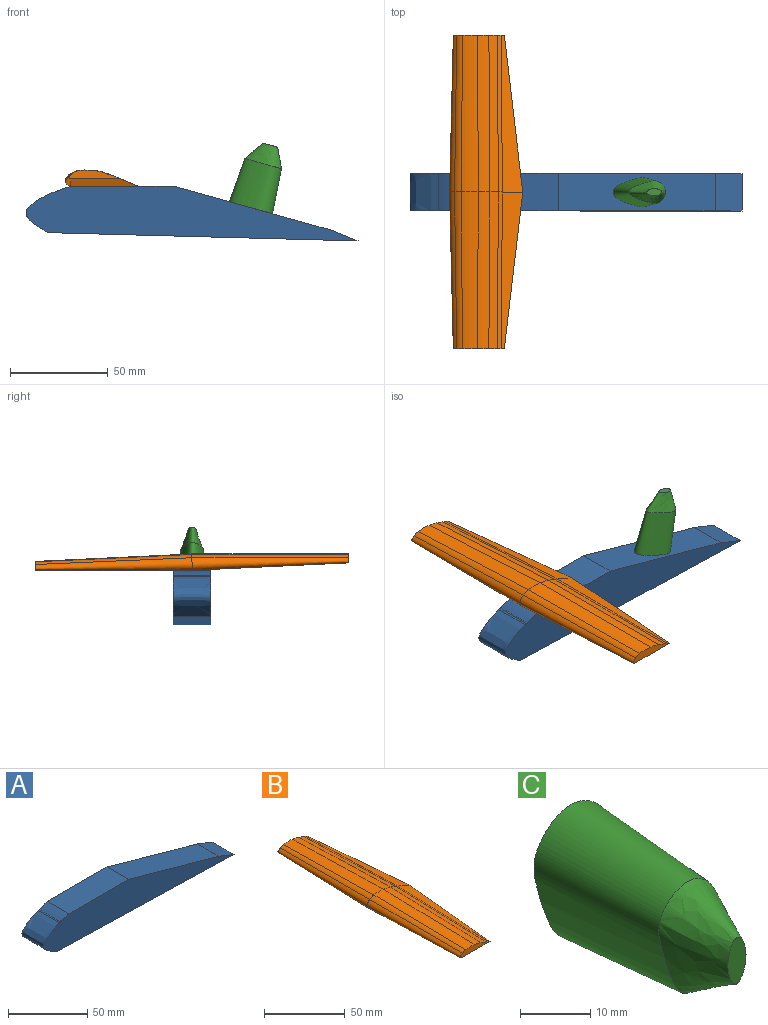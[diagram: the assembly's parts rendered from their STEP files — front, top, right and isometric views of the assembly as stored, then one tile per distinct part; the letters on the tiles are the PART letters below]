
ASSEMBLY  parts=3 mates=2
PART A: 10 faces, bbox 170.2x19.1x27.9 mm
  f0: extruded ~19.1x0.6mm, area 11.5mm2, adj f7,f8,f9
  f1: extruded ~20.69x19.1mm, area 650.4mm2, adj f2,f6,f8,f9
  f2: plane 158.3x19.1mm, normal (-0.03,0,-1), area 3024.7mm2, adj f1,f3,f8,f9
  f3: plane 19.1x13.75mm, normal (0.37,0,0.93), area 283mm2, adj f2,f4,f8,f9
  f4: plane 80.12x22.34mm, normal (0.27,0,0.96), area 1588.7mm2, adj f3,f5,f8,f9
  f5: plane 52.9x19.1mm, normal (0,0,1), area 1010.5mm2, adj f4,f6,f8,f9
  f6: extruded ~19.1x8.41mm, area 170.3mm2, adj f1,f5,f8,f9
  f7: plane 19.1x0.6mm, normal (0.1,0,-0.99), area 11.5mm2, adj f0,f8,f9
  f8: plane 170.24x27.9mm, normal (0,-1,0), area 2952.1mm2, adj f0,f1,f2,f3,f4,f5,f6,f7
  f9: plane 170.24x27.9mm, normal (0,1,0), area 2952.1mm2, adj f0,f1,f2,f3,f4,f5,f6,f7
PART B: 18 faces, bbox 37.4x160.1x8.5 mm
  f0: plane 26.14x4.82mm, normal (0,-1,0), area 83.7mm2, adj f1,f2,f3,f4,f5,f6,f7,f8
  f1: bspline ~80x3.96mm, area 284.8mm2, adj f0,f2,f8,f10
  f2: bspline ~80x8.47mm, area 656.7mm2, adj f0,f1,f3,f11
  f3: bspline ~80x6.26mm, area 481mm2, adj f0,f2,f4,f12
  f4: bspline ~80x4.93mm, area 364.4mm2, adj f0,f3,f5,f13
  f5: bspline ~80x2.73mm, area 172.5mm2, adj f0,f4,f6,f14
  f6: plane 80x11.06mm, normal (0.39,-0.02,0.92), area 523.9mm2, adj f0,f5,f7,f15
  f7: plane 80x34.83mm, normal (0,-0.02,-1), area 2399.5mm2, adj f0,f6,f8,f16
  f8: bspline ~80x6.42mm, area 512.4mm2, adj f0,f1,f7,f17
  f9: plane 26.14x4.82mm, normal (0,1,0), area 83.7mm2, adj f10,f11,f12,f13,f14,f15,f16,f17
  f10: bspline ~80x3.96mm, area 284.8mm2, adj f1,f9,f11,f17
  f11: bspline ~80x8.47mm, area 656.7mm2, adj f2,f9,f10,f12
  f12: bspline ~80x6.26mm, area 481mm2, adj f3,f9,f11,f13
  f13: bspline ~80x4.93mm, area 364.4mm2, adj f4,f9,f12,f14
  f14: bspline ~80x2.73mm, area 172.5mm2, adj f5,f9,f13,f15
  f15: plane 80x11.06mm, normal (0.39,0.02,0.92), area 523.9mm2, adj f6,f9,f14,f16
  f16: plane 80x34.83mm, normal (0,0.02,-1), area 2399.5mm2, adj f7,f9,f15,f17
  f17: bspline ~80x6.42mm, area 512.4mm2, adj f8,f9,f10,f16
PART C: 4 faces, bbox 15.1x33.7x23.1 mm
  f0: plane 23.07x15.15mm, normal (0,1,0), area 246.1mm2, adj f1
  f1: bspline ~23.4x22.66mm, area 1260.5mm2, adj f0,f3
  f2: plane 8.05x3.65mm, normal (0,-1,0), area 22.4mm2, adj f3
  f3: bspline ~19.32x11.45mm, area 360.7mm2, adj f1,f2
PLACE A t=(0.77,0,-34.56)mm
PLACE B rot(axis=(-0.98,-0.18,0),1.4deg) t=(-10.15,-10.07,4.32)mm
PLACE C rot(axis=(-0.62,0.62,-0.47),129.4deg) t=(14.76,-33.28,44.91)mm
MATE fastened B.f16 <-> A.f5  axis (0,0,-1) through (-57.54,-9.55,26.02)mm
MATE fastened C.f0 <-> A.f4  axis (-0.27,0,-0.96) through (35.43,-9.55,14.85)mm
